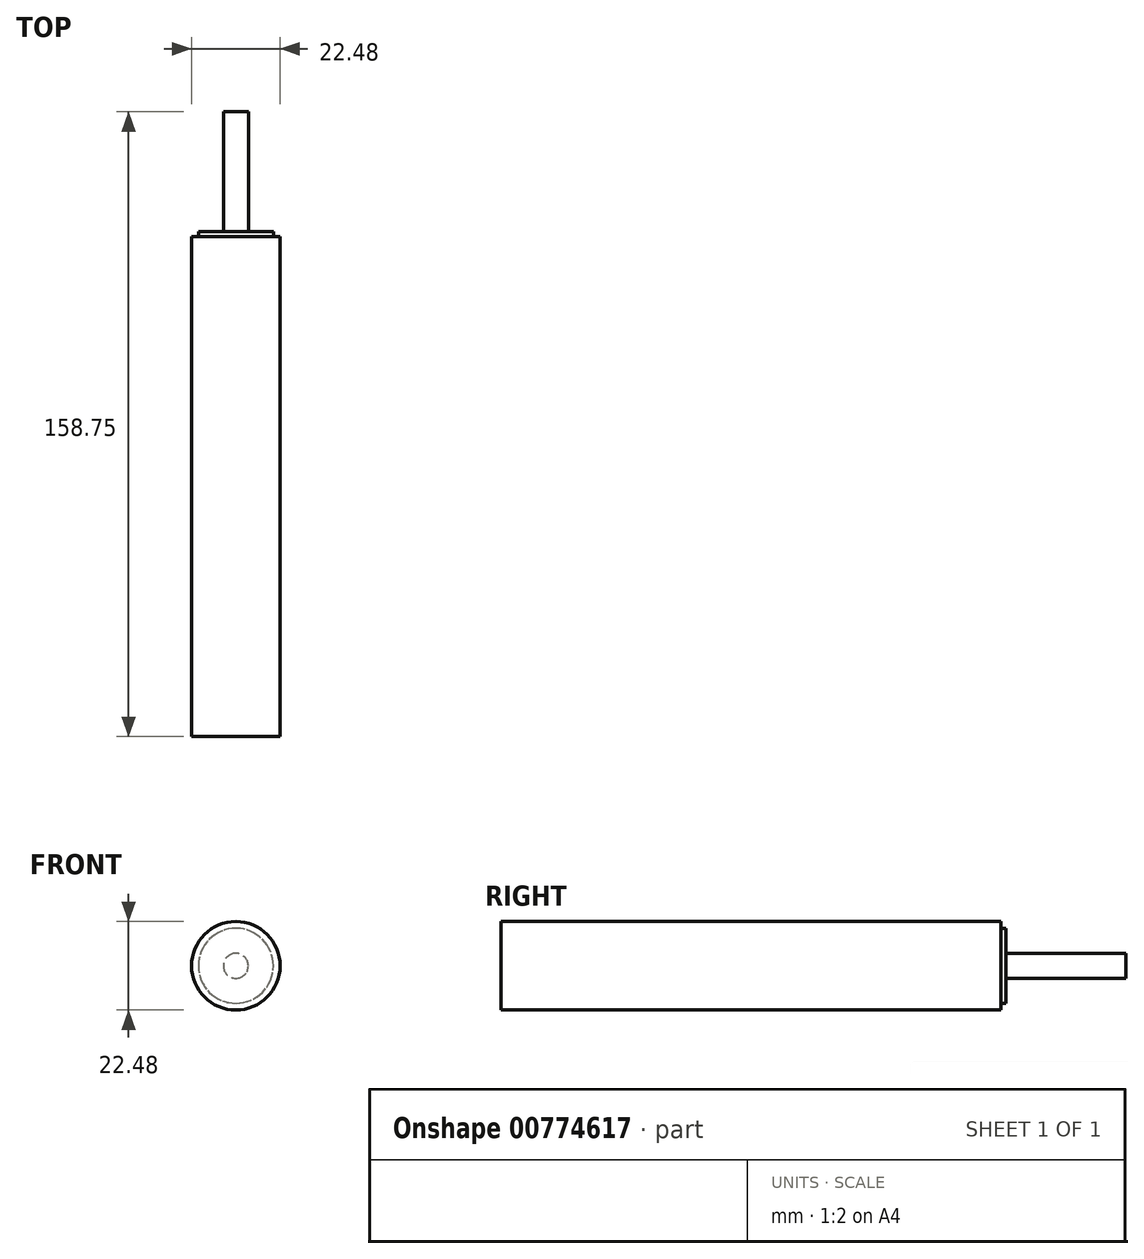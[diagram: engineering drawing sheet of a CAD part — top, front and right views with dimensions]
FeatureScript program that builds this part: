
annotation { "Feature Type Name" : "Feature", "Feature Type Description" : "" }
export const myFeature = defineFeature(function(context is Context, id is Id, definition is map)
    precondition{}
    {
        {
            var Q0;
            Q0=qCreatedBy(makeId("Front.planeOp"),FACE);
            var sketch = newSketch(context, id + "F0", { "sketchPlane" : qUnion([Q0])});
            skCircle(sketch, "E0", {"center": v(0, 0) * mm, "radius": 11.24 * mm});
            skSolve(sketch);
        }
        {
            var Q0;
            Q0=makeQuery(id+"F0.imprint","IMPRINT",FACE,{"disambiguationData":[TD([[makeQuery(id+"F0.imprint","IMPRINT",EDGE,{"derivedFrom":sQuery(id+"F0.wireOp",EDGE,"E0")}),1.0]])]});
            extrude(context, id + "F1", {"entities" : qUnion([Q0]), "depth" : 127 * mm, "offsetDistance" : 25.4 * mm});
        }
        {
            var Q0;
            Q0=qCreatedBy(makeId("Front.planeOp"),FACE);
            var sketch = newSketch(context, id + "F2", { "sketchPlane" : qUnion([Q0])});
            skCircle(sketch, "E1", {"center": v(0, 0) * mm, "radius": 3.18 * mm});
            skSolve(sketch);
        }
        {
            var Q0;
            Q0=makeQuery(id+"F2.imprint","IMPRINT",FACE,{"disambiguationData":[TD([[makeQuery(id+"F2.imprint","IMPRINT",EDGE,{"derivedFrom":sQuery(id+"F2.wireOp",EDGE,"E1")}),1.0]])]});
            extrude(context, id + "F3", {"entities" : qUnion([Q0]), "operationType" : NewBodyOperationType.ADD, "oppositeDirection" : true, "depth" : 31.75 * mm, "offsetDistance" : 25.4 * mm});
        }
        {
            var Q0;
            Q0=makeQuery(id+"F1.opExtrude","CAP_FACE",FACE,{"disambiguationData":[OSD([sQuery(id+"F0.wireOp",EDGE,"E0")])],"isStart":true});
            var sketch = newSketch(context, id + "F4", { "sketchPlane" : qUnion([Q0])});
            skCircle(sketch, "E2", {"center": v(0, 0) * mm, "radius": 9.52 * mm});
            skSolve(sketch);
        }
        {
            var Q0;
            Q0=makeQuery(id+"F4.imprint","IMPRINT",FACE,{"disambiguationData":[TD([[makeQuery(id+"F4.imprint","IMPRINT",EDGE,{"derivedFrom":sQuery(id+"F4.wireOp",EDGE,"E2")}),1.0]])]});
            extrude(context, id + "F5", {"entities" : qUnion([Q0]), "operationType" : NewBodyOperationType.ADD, "depth" : 1.27 * mm, "offsetDistance" : 25.4 * mm});
        }
    });
